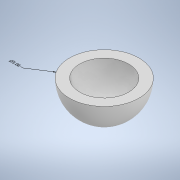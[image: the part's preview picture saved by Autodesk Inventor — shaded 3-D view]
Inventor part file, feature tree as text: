
AUTODESK INVENTOR PART (.ipt)
format: ipt  version: 2022 (Build 260153000, 153)  size: 154,624 bytes
history: native  units: in
note: dims shown in document units (in); Inventor stores cm internally (conversion verified against a paired STEP export)
features: other x2, revolve x1, thicken_offset x1, shell x1, sketch x1
ambient origin geometry x8: Origin, YZ Plane, XZ Plane, XY Plane, X Axis, Y Axis, Z Axis, Center Point
bodies: Solid1 (feature_tree)
feature tree (6):
  other  "Annotations"
  revolve  "Revolution1"  [1 undecoded]
  thicken_offset  "Thicken1"
  shell  "Shell1"  Thickness=1.03in
  sketch  "Sketch1"  dims[d3=90.0deg d6=1.03in d7=1.03in d8=0.75in d4=0.2255in d5=5.06in]
  other  "Diameter Dimension 1"
note: 1 required parameter value undecoded (feature->parameter linkage not recoverable at this tier; creation-order binding heuristic only, values carry confidence <= 0.55)
